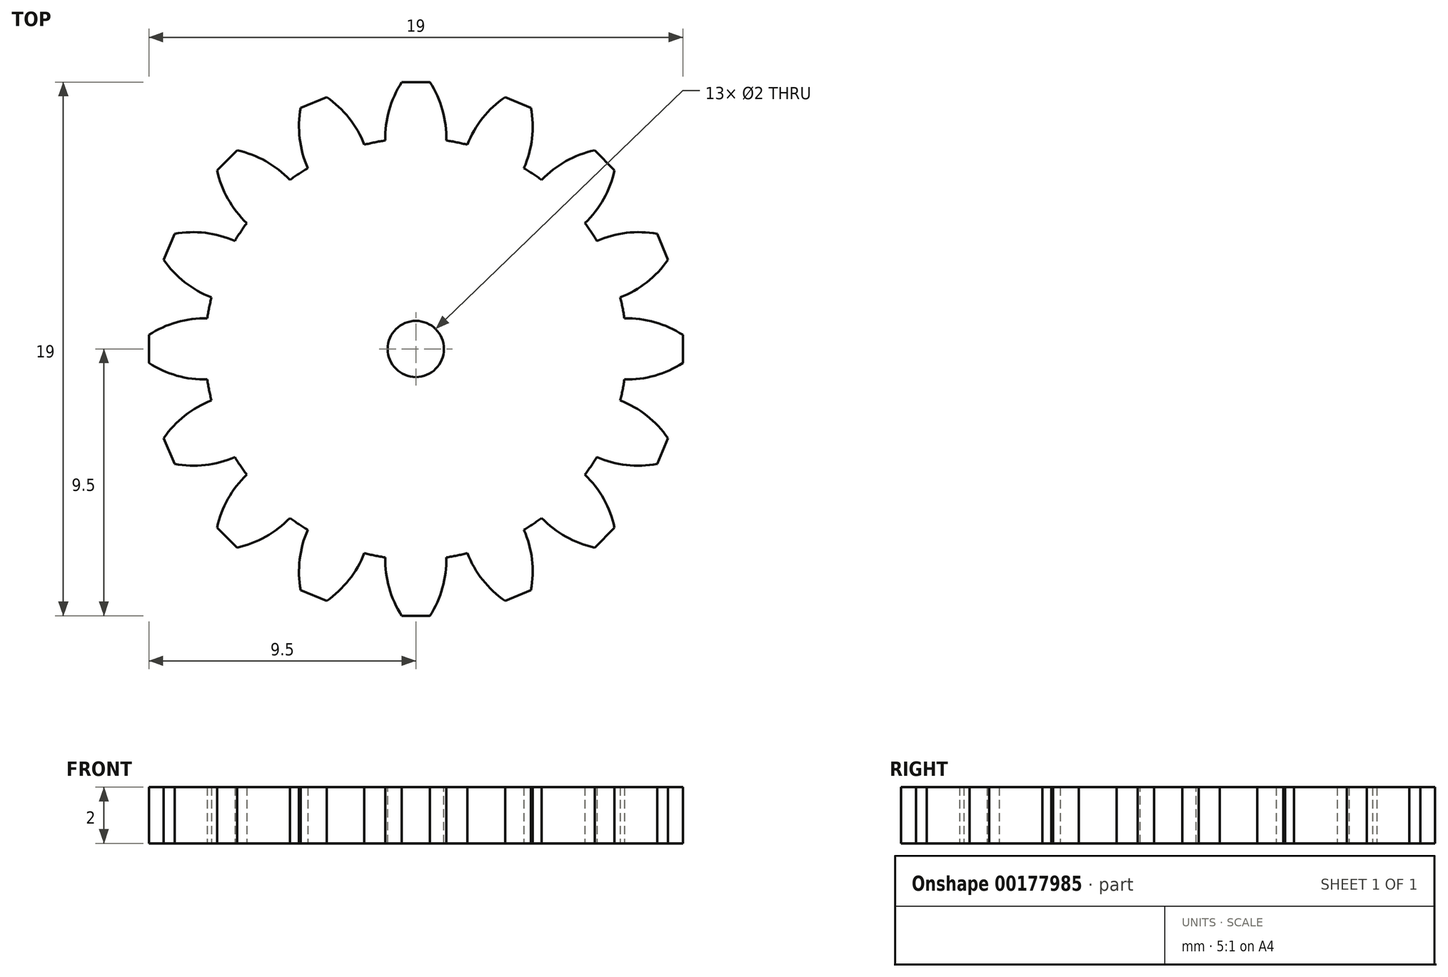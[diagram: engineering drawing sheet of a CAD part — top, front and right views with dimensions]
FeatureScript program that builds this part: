
annotation { "Feature Type Name" : "Feature", "Feature Type Description" : "" }
export const myFeature = defineFeature(function(context is Context, id is Id, definition is map)
    precondition{}
    {
        {
            var Q0;
            Q0=qCreatedBy(makeId("Top.planeOp"),FACE);
            var sketch = newSketch(context, id + "F0", { "sketchPlane" : qUnion([Q0])});
            skCircle(sketch, "E0", {"center": v(0, 0) * mm, "radius": 7.5 * mm});
            skLineSegment(sketch, "E1", {"start": v(0, 0) * mm, "end": v(0, 7.5) * mm, "construction": true});
            skLineSegment(sketch, "E2", {"start": v(0, 9.5) * mm, "end": v(-0.5, 9.5) * mm});
            skArc(sketch, "E3", {"start": v(-0.5, 9.5) * mm, "mid": v(-0.95, 8.5) * mm, "end": v(-1.09, 7.42) * mm});
            skLineSegment(sketch, "E4.MirrorCS", {"start": v(0, 9.5) * mm, "end": v(0.5, 9.5) * mm});
            skArc(sketch, "E5.MirrorCS", {"start": v(0.5, 9.5) * mm, "mid": v(0.95, 8.5) * mm, "end": v(1.09, 7.42) * mm});
            skArc(sketch, "E6.1.0", {"start": v(-4.1, 8.59) * mm, "mid": v(-4.13, 7.5) * mm, "end": v(-3.85, 6.44) * mm});
            skLineSegment(sketch, "E6.1.1", {"start": v(-3.64, 8.78) * mm, "end": v(-4.1, 8.59) * mm});
            skLineSegment(sketch, "E6.1.2", {"start": v(-3.64, 8.78) * mm, "end": v(-3.17, 8.97) * mm});
            skArc(sketch, "E6.1.3", {"start": v(-3.17, 8.97) * mm, "mid": v(-2.38, 8.22) * mm, "end": v(-1.83, 7.27) * mm});
            skArc(sketch, "E6.2.0", {"start": v(-7.07, 6.36) * mm, "mid": v(-6.69, 5.34) * mm, "end": v(-6.02, 4.48) * mm});
            skLineSegment(sketch, "E6.2.1", {"start": v(-6.72, 6.72) * mm, "end": v(-7.07, 6.36) * mm});
            skLineSegment(sketch, "E6.2.2", {"start": v(-6.72, 6.72) * mm, "end": v(-6.36, 7.07) * mm});
            skArc(sketch, "E6.2.3", {"start": v(-6.36, 7.07) * mm, "mid": v(-5.34, 6.69) * mm, "end": v(-4.48, 6.02) * mm});
            skArc(sketch, "E6.3.0", {"start": v(-8.97, 3.17) * mm, "mid": v(-8.22, 2.38) * mm, "end": v(-7.27, 1.83) * mm});
            skLineSegment(sketch, "E6.3.1", {"start": v(-8.78, 3.64) * mm, "end": v(-8.97, 3.17) * mm});
            skLineSegment(sketch, "E6.3.2", {"start": v(-8.78, 3.64) * mm, "end": v(-8.59, 4.1) * mm});
            skArc(sketch, "E6.3.3", {"start": v(-8.59, 4.1) * mm, "mid": v(-7.5, 4.13) * mm, "end": v(-6.44, 3.85) * mm});
            skArc(sketch, "E6.4.0", {"start": v(-9.5, -0.5) * mm, "mid": v(-8.5, -0.95) * mm, "end": v(-7.42, -1.09) * mm});
            skLineSegment(sketch, "E6.4.1", {"start": v(-9.5, 0) * mm, "end": v(-9.5, -0.5) * mm});
            skLineSegment(sketch, "E6.4.2", {"start": v(-9.5, 0) * mm, "end": v(-9.5, 0.5) * mm});
            skArc(sketch, "E6.4.3", {"start": v(-9.5, 0.5) * mm, "mid": v(-8.5, 0.95) * mm, "end": v(-7.42, 1.09) * mm});
            skArc(sketch, "E6.5.0", {"start": v(-8.59, -4.1) * mm, "mid": v(-7.5, -4.13) * mm, "end": v(-6.44, -3.85) * mm});
            skLineSegment(sketch, "E6.5.1", {"start": v(-8.78, -3.64) * mm, "end": v(-8.59, -4.1) * mm});
            skLineSegment(sketch, "E6.5.2", {"start": v(-8.78, -3.64) * mm, "end": v(-8.97, -3.17) * mm});
            skArc(sketch, "E6.5.3", {"start": v(-8.97, -3.17) * mm, "mid": v(-8.22, -2.38) * mm, "end": v(-7.27, -1.83) * mm});
            skArc(sketch, "E6.6.0", {"start": v(-6.36, -7.07) * mm, "mid": v(-5.34, -6.69) * mm, "end": v(-4.48, -6.02) * mm});
            skLineSegment(sketch, "E6.6.1", {"start": v(-6.72, -6.72) * mm, "end": v(-6.36, -7.07) * mm});
            skLineSegment(sketch, "E6.6.2", {"start": v(-6.72, -6.72) * mm, "end": v(-7.07, -6.36) * mm});
            skArc(sketch, "E6.6.3", {"start": v(-7.07, -6.36) * mm, "mid": v(-6.69, -5.34) * mm, "end": v(-6.02, -4.48) * mm});
            skArc(sketch, "E6.7.0", {"start": v(-3.17, -8.97) * mm, "mid": v(-2.38, -8.22) * mm, "end": v(-1.83, -7.27) * mm});
            skLineSegment(sketch, "E6.7.1", {"start": v(-3.64, -8.78) * mm, "end": v(-3.17, -8.97) * mm});
            skLineSegment(sketch, "E6.7.2", {"start": v(-3.64, -8.78) * mm, "end": v(-4.1, -8.59) * mm});
            skArc(sketch, "E6.7.3", {"start": v(-4.1, -8.59) * mm, "mid": v(-4.13, -7.5) * mm, "end": v(-3.85, -6.44) * mm});
            skArc(sketch, "E6.8.0", {"start": v(0.5, -9.5) * mm, "mid": v(0.95, -8.5) * mm, "end": v(1.09, -7.42) * mm});
            skLineSegment(sketch, "E6.8.1", {"start": v(0, -9.5) * mm, "end": v(0.5, -9.5) * mm});
            skLineSegment(sketch, "E6.8.2", {"start": v(0, -9.5) * mm, "end": v(-0.5, -9.5) * mm});
            skArc(sketch, "E6.8.3", {"start": v(-0.5, -9.5) * mm, "mid": v(-0.95, -8.5) * mm, "end": v(-1.09, -7.42) * mm});
            skArc(sketch, "E6.9.0", {"start": v(4.1, -8.59) * mm, "mid": v(4.13, -7.5) * mm, "end": v(3.85, -6.44) * mm});
            skLineSegment(sketch, "E6.9.1", {"start": v(3.64, -8.78) * mm, "end": v(4.1, -8.59) * mm});
            skLineSegment(sketch, "E6.9.2", {"start": v(3.64, -8.78) * mm, "end": v(3.17, -8.97) * mm});
            skArc(sketch, "E6.9.3", {"start": v(3.17, -8.97) * mm, "mid": v(2.38, -8.22) * mm, "end": v(1.83, -7.27) * mm});
            skArc(sketch, "E6.10.0", {"start": v(7.07, -6.36) * mm, "mid": v(6.69, -5.34) * mm, "end": v(6.02, -4.48) * mm});
            skLineSegment(sketch, "E6.10.1", {"start": v(6.72, -6.72) * mm, "end": v(7.07, -6.36) * mm});
            skLineSegment(sketch, "E6.10.2", {"start": v(6.72, -6.72) * mm, "end": v(6.36, -7.07) * mm});
            skArc(sketch, "E6.10.3", {"start": v(6.36, -7.07) * mm, "mid": v(5.34, -6.69) * mm, "end": v(4.48, -6.02) * mm});
            skArc(sketch, "E6.11.0", {"start": v(8.97, -3.17) * mm, "mid": v(8.22, -2.38) * mm, "end": v(7.27, -1.83) * mm});
            skLineSegment(sketch, "E6.11.1", {"start": v(8.78, -3.64) * mm, "end": v(8.97, -3.17) * mm});
            skLineSegment(sketch, "E6.11.2", {"start": v(8.78, -3.64) * mm, "end": v(8.59, -4.1) * mm});
            skArc(sketch, "E6.11.3", {"start": v(8.59, -4.1) * mm, "mid": v(7.5, -4.13) * mm, "end": v(6.44, -3.85) * mm});
            skArc(sketch, "E6.12.0", {"start": v(9.5, 0.5) * mm, "mid": v(8.5, 0.95) * mm, "end": v(7.42, 1.09) * mm});
            skLineSegment(sketch, "E6.12.1", {"start": v(9.5, 0) * mm, "end": v(9.5, 0.5) * mm});
            skLineSegment(sketch, "E6.12.2", {"start": v(9.5, 0) * mm, "end": v(9.5, -0.5) * mm});
            skArc(sketch, "E6.12.3", {"start": v(9.5, -0.5) * mm, "mid": v(8.5, -0.95) * mm, "end": v(7.42, -1.09) * mm});
            skArc(sketch, "E6.13.0", {"start": v(8.59, 4.1) * mm, "mid": v(7.5, 4.13) * mm, "end": v(6.44, 3.85) * mm});
            skLineSegment(sketch, "E6.13.1", {"start": v(8.78, 3.64) * mm, "end": v(8.59, 4.1) * mm});
            skLineSegment(sketch, "E6.13.2", {"start": v(8.78, 3.64) * mm, "end": v(8.97, 3.17) * mm});
            skArc(sketch, "E6.13.3", {"start": v(8.97, 3.17) * mm, "mid": v(8.22, 2.38) * mm, "end": v(7.27, 1.83) * mm});
            skArc(sketch, "E6.14.0", {"start": v(6.36, 7.07) * mm, "mid": v(5.34, 6.69) * mm, "end": v(4.48, 6.02) * mm});
            skLineSegment(sketch, "E6.14.1", {"start": v(6.72, 6.72) * mm, "end": v(6.36, 7.07) * mm});
            skLineSegment(sketch, "E6.14.2", {"start": v(6.72, 6.72) * mm, "end": v(7.07, 6.36) * mm});
            skArc(sketch, "E6.14.3", {"start": v(7.07, 6.36) * mm, "mid": v(6.69, 5.34) * mm, "end": v(6.02, 4.48) * mm});
            skArc(sketch, "E6.15.0", {"start": v(3.17, 8.97) * mm, "mid": v(2.38, 8.22) * mm, "end": v(1.83, 7.27) * mm});
            skLineSegment(sketch, "E6.15.1", {"start": v(3.64, 8.78) * mm, "end": v(3.17, 8.97) * mm});
            skLineSegment(sketch, "E6.15.2", {"start": v(3.64, 8.78) * mm, "end": v(4.1, 8.59) * mm});
            skArc(sketch, "E6.15.3", {"start": v(4.1, 8.59) * mm, "mid": v(4.13, 7.5) * mm, "end": v(3.85, 6.44) * mm});
            skSolve(sketch);
        }
        {
            var Q0;
            Q0 = qSketchRegion(id + "F0", true);
            extrude(context, id + "F1", {"entities" : qUnion([Q0]), "depth" : 2 * mm});
        }
        {
            var Q0;
            Q0=makeQuery(id+"F1.opExtrude","CAP_FACE",FACE,{"disambiguationData":[OSD([sQuery(id+"F0.wireOp",EDGE,"E0"),sQuery(id+"F0.wireOp",EDGE,"E2"),sQuery(id+"F0.wireOp",EDGE,"E3"),sQuery(id+"F0.wireOp",EDGE,"E4.MirrorCS"),sQuery(id+"F0.wireOp",EDGE,"E5.MirrorCS"),sQuery(id+"F0.wireOp",EDGE,"E6.1.0"),sQuery(id+"F0.wireOp",EDGE,"E6.1.1"),sQuery(id+"F0.wireOp",EDGE,"E6.1.2"),sQuery(id+"F0.wireOp",EDGE,"E6.1.3"),sQuery(id+"F0.wireOp",EDGE,"E6.2.0"),sQuery(id+"F0.wireOp",EDGE,"E6.2.1"),sQuery(id+"F0.wireOp",EDGE,"E6.2.2"),sQuery(id+"F0.wireOp",EDGE,"E6.2.3"),sQuery(id+"F0.wireOp",EDGE,"E6.3.0"),sQuery(id+"F0.wireOp",EDGE,"E6.3.1"),sQuery(id+"F0.wireOp",EDGE,"E6.3.2"),sQuery(id+"F0.wireOp",EDGE,"E6.3.3"),sQuery(id+"F0.wireOp",EDGE,"E6.4.0"),sQuery(id+"F0.wireOp",EDGE,"E6.4.1"),sQuery(id+"F0.wireOp",EDGE,"E6.4.2"),sQuery(id+"F0.wireOp",EDGE,"E6.4.3"),sQuery(id+"F0.wireOp",EDGE,"E6.5.0"),sQuery(id+"F0.wireOp",EDGE,"E6.5.1"),sQuery(id+"F0.wireOp",EDGE,"E6.5.2"),sQuery(id+"F0.wireOp",EDGE,"E6.5.3"),sQuery(id+"F0.wireOp",EDGE,"E6.6.0"),sQuery(id+"F0.wireOp",EDGE,"E6.6.1"),sQuery(id+"F0.wireOp",EDGE,"E6.6.2"),sQuery(id+"F0.wireOp",EDGE,"E6.6.3"),sQuery(id+"F0.wireOp",EDGE,"E6.7.0"),sQuery(id+"F0.wireOp",EDGE,"E6.7.1"),sQuery(id+"F0.wireOp",EDGE,"E6.7.2"),sQuery(id+"F0.wireOp",EDGE,"E6.7.3"),sQuery(id+"F0.wireOp",EDGE,"E6.8.0"),sQuery(id+"F0.wireOp",EDGE,"E6.8.1"),sQuery(id+"F0.wireOp",EDGE,"E6.8.2"),sQuery(id+"F0.wireOp",EDGE,"E6.8.3"),sQuery(id+"F0.wireOp",EDGE,"E6.9.0"),sQuery(id+"F0.wireOp",EDGE,"E6.9.1"),sQuery(id+"F0.wireOp",EDGE,"E6.9.2"),sQuery(id+"F0.wireOp",EDGE,"E6.9.3"),sQuery(id+"F0.wireOp",EDGE,"E6.10.0"),sQuery(id+"F0.wireOp",EDGE,"E6.10.1"),sQuery(id+"F0.wireOp",EDGE,"E6.10.2"),sQuery(id+"F0.wireOp",EDGE,"E6.10.3"),sQuery(id+"F0.wireOp",EDGE,"E6.11.0"),sQuery(id+"F0.wireOp",EDGE,"E6.11.1"),sQuery(id+"F0.wireOp",EDGE,"E6.11.2"),sQuery(id+"F0.wireOp",EDGE,"E6.11.3"),sQuery(id+"F0.wireOp",EDGE,"E6.12.0"),sQuery(id+"F0.wireOp",EDGE,"E6.12.1"),sQuery(id+"F0.wireOp",EDGE,"E6.12.2"),sQuery(id+"F0.wireOp",EDGE,"E6.12.3"),sQuery(id+"F0.wireOp",EDGE,"E6.13.0"),sQuery(id+"F0.wireOp",EDGE,"E6.13.1"),sQuery(id+"F0.wireOp",EDGE,"E6.13.2"),sQuery(id+"F0.wireOp",EDGE,"E6.13.3"),sQuery(id+"F0.wireOp",EDGE,"E6.14.0"),sQuery(id+"F0.wireOp",EDGE,"E6.14.1"),sQuery(id+"F0.wireOp",EDGE,"E6.14.2"),sQuery(id+"F0.wireOp",EDGE,"E6.14.3"),sQuery(id+"F0.wireOp",EDGE,"E6.15.0"),sQuery(id+"F0.wireOp",EDGE,"E6.15.1"),sQuery(id+"F0.wireOp",EDGE,"E6.15.2"),sQuery(id+"F0.wireOp",EDGE,"E6.15.3")])],"isStart":false});
            var sketch = newSketch(context, id + "F2", { "sketchPlane" : qUnion([Q0])});
            skCircle(sketch, "E7", {"center": v(0, 0) * mm, "radius": 1 * mm});
            skSolve(sketch);
        }
        {
            var Q0;
            Q0=makeQuery(id+"F2.imprint","IMPRINT",FACE,{"disambiguationData":[TD([[makeQuery(id+"F2.imprint","IMPRINT",EDGE,{"derivedFrom":sQuery(id+"F2.wireOp",EDGE,"E7")}),1.0]])]});
            extrude(context, id + "F3", {"entities" : qUnion([Q0]), "operationType" : NewBodyOperationType.REMOVE, "endBound" : BoundingType.THROUGH_ALL, "oppositeDirection" : true, "depth" : 25 * mm});
        }
    });
